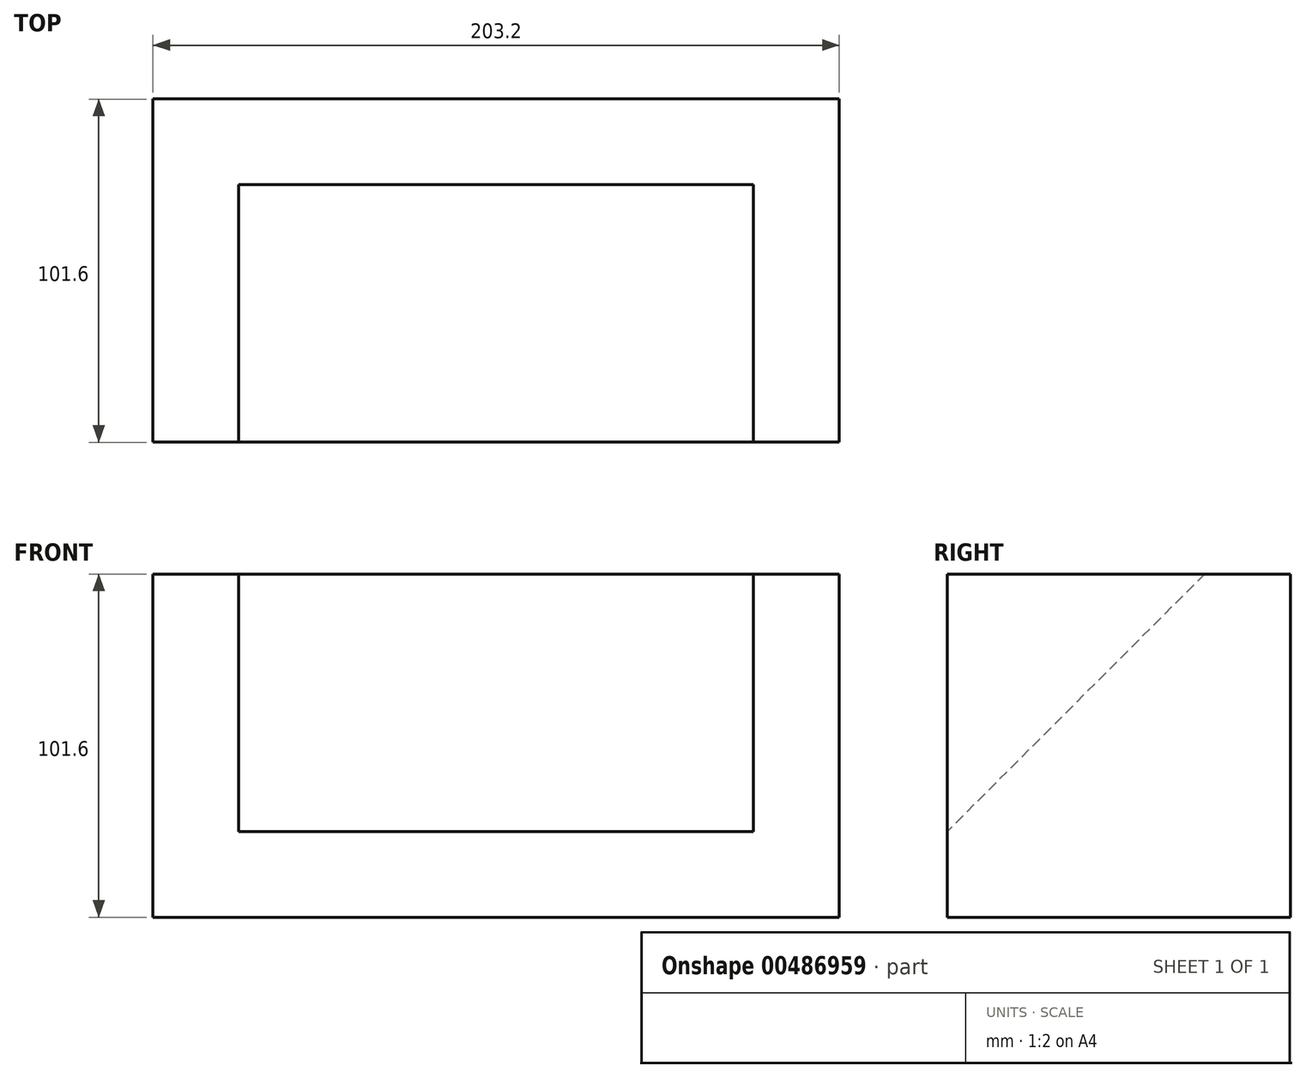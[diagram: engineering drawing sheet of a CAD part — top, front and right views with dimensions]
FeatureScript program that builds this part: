
annotation { "Feature Type Name" : "Feature", "Feature Type Description" : "" }
export const myFeature = defineFeature(function(context is Context, id is Id, definition is map)
    precondition{}
    {
        {
            var Q0;
            Q0=qCreatedBy(makeId("Top.planeOp"),FACE);
            var sketch = newSketch(context, id + "F0", { "sketchPlane" : qUnion([Q0])});
            skLineSegment(sketch, "E0.bottom", {"start": v(-147.48, 72.1) * mm, "end": v(55.72, 72.1) * mm});
            skLineSegment(sketch, "E0.top", {"start": v(-147.48, -29.5) * mm, "end": v(55.72, -29.5) * mm});
            skLineSegment(sketch, "E0.left", {"start": v(-147.48, 72.1) * mm, "end": v(-147.48, -29.5) * mm});
            skLineSegment(sketch, "E0.right", {"start": v(55.72, 72.1) * mm, "end": v(55.72, -29.5) * mm});
            skSolve(sketch);
        }
        {
            var Q0;
            Q0=qSketchRegion(id+"F0",true);
            extrude(context, id + "F1", {"entities" : qUnion([Q0]), "depth" : 101.6 * mm});
        }
        {
            var Q0;
            Q0=makeQuery(id+"F1.opExtrude","CAP_FACE",FACE,{"disambiguationData":[OSD([sQuery(id+"F0.wireOp",EDGE,"E0.bottom"),sQuery(id+"F0.wireOp",EDGE,"E0.top"),sQuery(id+"F0.wireOp",EDGE,"E0.left"),sQuery(id+"F0.wireOp",EDGE,"E0.right")])],"isStart":false});
            var sketch = newSketch(context, id + "F2", { "sketchPlane" : qUnion([Q0])});
            skLineSegment(sketch, "E1.bottom", {"start": v(-122.08, -29.5) * mm, "end": v(30.32, -29.5) * mm});
            skLineSegment(sketch, "E1.top", {"start": v(-122.08, 46.7) * mm, "end": v(30.32, 46.7) * mm});
            skLineSegment(sketch, "E1.left", {"start": v(-122.08, -29.5) * mm, "end": v(-122.08, 46.7) * mm});
            skLineSegment(sketch, "E1.right", {"start": v(30.32, -29.5) * mm, "end": v(30.32, 46.7) * mm});
            skSolve(sketch);
        }
        {
            var Q0;
            Q0=qSketchRegion(id+"F2",true);
            extrude(context, id + "F3", {"entities" : qUnion([Q0]), "operationType" : NewBodyOperationType.REMOVE, "oppositeDirection" : true, "depth" : 76.2 * mm});
        }
        {
            var Q0;
            Q0=makeQuery(id+"F3.boolean.opBoolean","COPY",FACE,{"derivedFrom":makeQuery(id+"F3.opExtrude","SWEPT_FACE",FACE,{"disambiguationData":[OSD([sQuery(id+"F2.wireOp",EDGE,"E1.left")])]})});
            var sketch = newSketch(context, id + "F4", { "sketchPlane" : qUnion([Q0])});
            skLineSegment(sketch, "E2", {"start": v(46.7, 101.6) * mm, "end": v(-29.5, 25.4) * mm});
            skSolve(sketch);
        }
        {
            var Q0;
            Q0 = qSketchRegion(id + "F4", true);
            var Q1;
            Q1=makeQuery(id+"F4.imprint","IMPRINT",FACE,{"disambiguationData":[TD([[makeQuery(id+"F4.imprint","IMPRINT",EDGE,{"derivedFrom":sQuery(id+"F4.wireOp",EDGE,"E2")}),1.0]])]});
            extrude(context, id + "F5", {"entities" : qUnion([Q0, Q1]), "operationType" : NewBodyOperationType.ADD, "depth" : 152.4 * mm});
        }
    });
